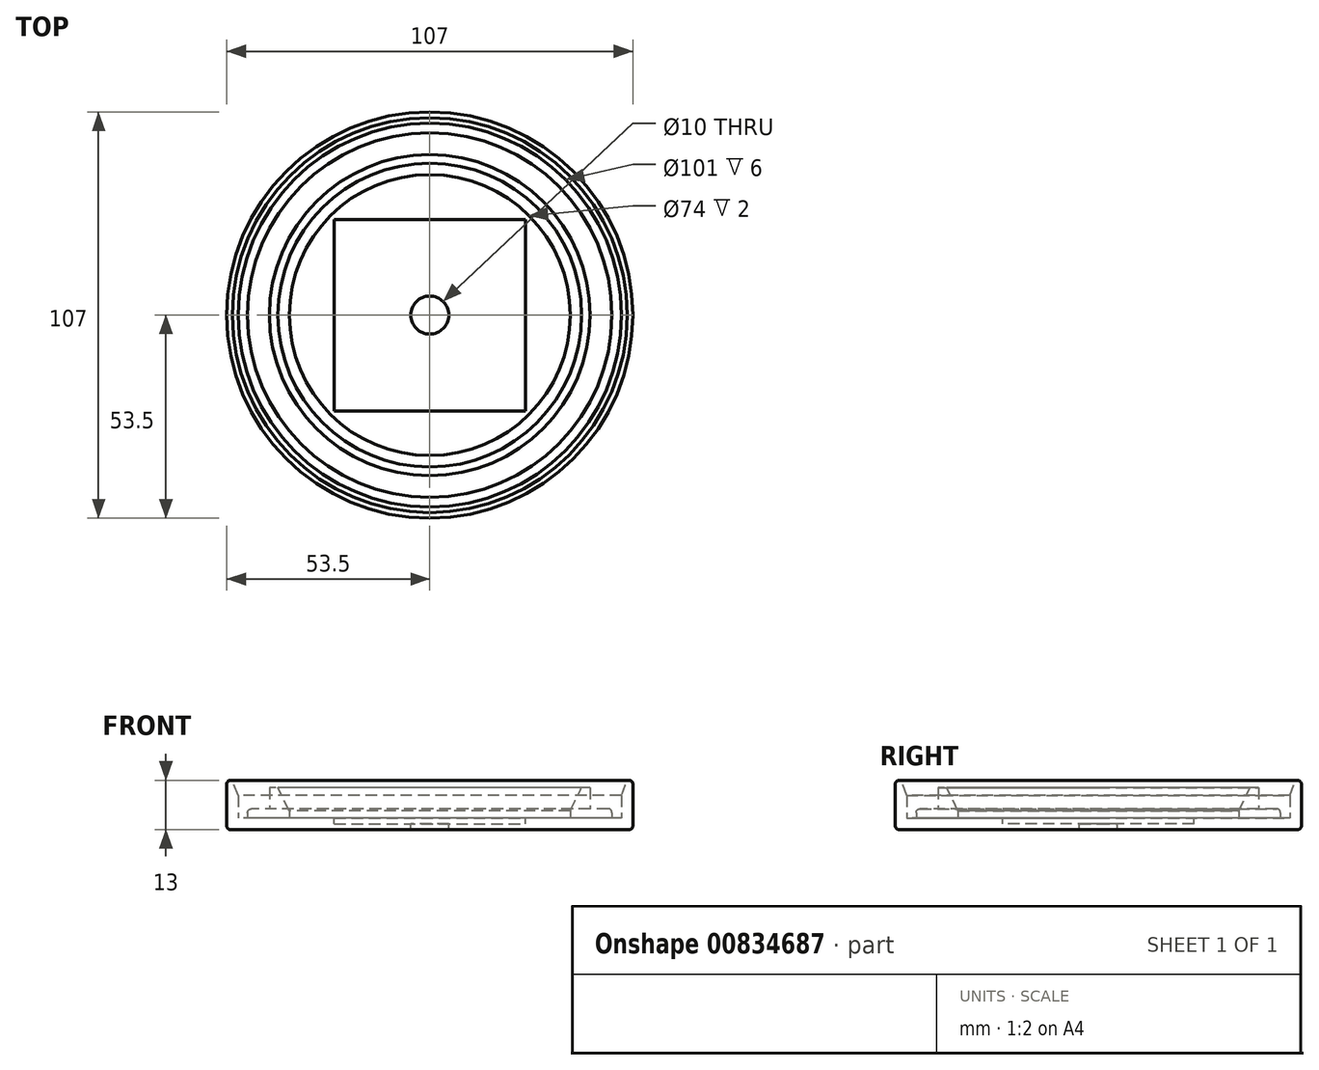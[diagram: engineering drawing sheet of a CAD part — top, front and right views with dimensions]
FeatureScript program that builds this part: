
annotation { "Feature Type Name" : "Feature", "Feature Type Description" : "" }
export const myFeature = defineFeature(function(context is Context, id is Id, definition is map)
    precondition{}
    {
        {
            var Q0;
            Q0=qCreatedBy(makeId("Top.planeOp"),FACE);
            var sketch = newSketch(context, id + "F0", { "sketchPlane" : qUnion([Q0])});
            skCircle(sketch, "E0", {"center": v(0, 0) * mm, "radius": 53.5 * mm});
            skSolve(sketch);
        }
        {
            var Q0;
            Q0=makeQuery(id+"F0.imprint","IMPRINT",FACE,{"disambiguationData":[TD([[makeQuery(id+"F0.imprint","IMPRINT",EDGE,{"derivedFrom":sQuery(id+"F0.wireOp",EDGE,"E0")}),1.0]])]});
            extrude(context, id + "F1", {"entities" : qUnion([Q0]), "depth" : 13 * mm, "offsetDistance" : 25 * mm});
        }
        {
            var Q0;
            Q0=makeQuery(id+"F1.opExtrude","CAP_FACE",FACE,{"disambiguationData":[OSD([sQuery(id+"F0.wireOp",EDGE,"E0")])],"isStart":false});
            shell(context, id + "F2", {"entities" : qUnion([Q0]), "thickness" : 3 * mm});
        }
        {
            var Q0;
            {var subQ0=sQuery(id+"F0.wireOp",EDGE,"E0");Q0=makeQuery(id+"F2.opShell","OFFSET_FACE",FACE,{"disambiguationData":[OSD([subQ0]),TDD([makeQuery(id+"F1.opExtrude","CAP_FACE",FACE,{"disambiguationData":[OSD([subQ0])],"isStart":true})])]});}
            var sketch = newSketch(context, id + "F3", { "sketchPlane" : qUnion([Q0])});
            skCircle(sketch, "E1", {"center": v(0, 0) * mm, "radius": 48 * mm});
            skCircle(sketch, "E2", {"center": v(0, 0) * mm, "radius": 42.25 * mm});
            skCircle(sketch, "E3", {"center": v(0, 0) * mm, "radius": 37 * mm});
            skSolve(sketch);
        }
        {
            var Q0;
            Q0=makeQuery(id+"F3.imprint","IMPRINT",FACE,{"disambiguationData":[TD([[makeQuery(id+"F3.imprint","IMPRINT",EDGE,{"derivedFrom":sQuery(id+"F3.wireOp",EDGE,"E1")}),1.0]])]});
            var Q1;
            Q1=makeQuery(id+"F3.imprint","IMPRINT",FACE,{"disambiguationData":[TD([[makeQuery(id+"F3.imprint","IMPRINT",EDGE,{"derivedFrom":sQuery(id+"F3.wireOp",EDGE,"E2")}),1.0]])]});
            extrude(context, id + "F4", {"entities" : qUnion([Q0, Q1]), "operationType" : NewBodyOperationType.ADD, "depth" : 2.5 * mm, "offsetDistance" : 25 * mm});
        }
        {
            var Q0;
            Q0=makeQuery(id+"F3.imprint","IMPRINT",FACE,{"disambiguationData":[TD([[makeQuery(id+"F3.imprint","IMPRINT",EDGE,{"derivedFrom":sQuery(id+"F3.wireOp",EDGE,"E2")}),1.0]])]});
            extrude(context, id + "F5", {"entities" : qUnion([Q0]), "operationType" : NewBodyOperationType.ADD, "depth" : 8 * mm, "offsetDistance" : 25 * mm});
        }
        {
            var Q0;
            Q0=makeQuery(id+"F5.opExtrude","CAP_EDGE",EDGE,{"disambiguationData":[OSD([sQuery(id+"F3.wireOp",EDGE,"E3")])],"isStart":false});
            chamfer(context, id + "F6", {"entities" : qUnion([Q0]), "chamferType" : ChamferType.TWO_OFFSETS, "width1" : 3 * mm, "oppositeDirection" : true, "width2" : 6 * mm, "tangentPropagation" : true});
        }
        {
            var Q0;
            {var subQ0=sQuery(id+"F0.wireOp",EDGE,"E0");Q0=makeQuery(id+"F2.opShell","OFFSET_EDGE",EDGE,{"disambiguationData":[OSD([subQ0]),TDD([makeQuery(id+"F1.opExtrude","CAP_EDGE",EDGE,{"disambiguationData":[OSD([subQ0])],"isStart":false})])]});}
            chamfer(context, id + "F7", {"entities" : qUnion([Q0]), "chamferType" : ChamferType.TWO_OFFSETS, "width1" : 4 * mm, "oppositeDirection" : false, "width2" : 1.5 * mm, "tangentPropagation" : true});
        }
        {
            var Q0;
            Q0=makeQuery(id+"F4.opExtrude","CAP_EDGE",EDGE,{"disambiguationData":[OSD([sQuery(id+"F3.wireOp",EDGE,"E1")])],"isStart":false});
            var Q1;
            Q1=makeQuery(id+"F1.opExtrude","CAP_EDGE",EDGE,{"disambiguationData":[OSD([sQuery(id+"F0.wireOp",EDGE,"E0")])],"isStart":true});
            var Q2;
            Q2=makeQuery(id+"F1.opExtrude","CAP_EDGE",EDGE,{"disambiguationData":[OSD([sQuery(id+"F0.wireOp",EDGE,"E0")])],"isStart":false});
            fillet(context, id + "F8", {"entities" : qUnion([Q0, Q1, Q2]), "radius" : 1 * mm, "tangentPropagation" : true, "allowEdgeOverflow" : false});
        }
        {
            var Q0;
            Q0=makeQuery(id+"F4.opExtrude","CAP_FACE",FACE,{"disambiguationData":[OSD([sQuery(id+"F3.wireOp",EDGE,"E1")])],"isStart":false});
            var sketch = newSketch(context, id + "F9", { "sketchPlane" : qUnion([Q0])});
            skCircle(sketch, "E4", {"center": v(0, 0) * mm, "radius": 5 * mm});
            skSolve(sketch);
        }
        {
            var Q0;
            Q0=qSketchRegion(id+"F9",true);
            extrude(context, id + "F10", {"entities" : qUnion([Q0]), "operationType" : NewBodyOperationType.REMOVE, "endBound" : BoundingType.SYMMETRIC, "oppositeDirection" : true, "depth" : 91.4 * mm, "offsetDistance" : 25 * mm});
        }
        {
            var Q0;
            Q0=makeQuery(id+"F3.imprint","IMPRINT",FACE,{"disambiguationData":[TD([[makeQuery(id+"F3.imprint","IMPRINT",EDGE,{"derivedFrom":sQuery(id+"F3.wireOp",EDGE,"E3")}),1.0]])]});
            var sketch = newSketch(context, id + "F11", { "sketchPlane" : qUnion([Q0])});
            skLineSegment(sketch, "E5.bottom", {"start": v(-25.2, 25.2) * mm, "end": v(25.2, 25.2) * mm});
            skLineSegment(sketch, "E5.top", {"start": v(-25.2, -25.2) * mm, "end": v(25.2, -25.2) * mm});
            skLineSegment(sketch, "E5.left", {"start": v(-25.2, 25.2) * mm, "end": v(-25.2, -25.2) * mm});
            skLineSegment(sketch, "E5.right", {"start": v(25.2, 25.2) * mm, "end": v(25.2, -25.2) * mm});
            skPoint(sketch, "E5.middle", {"position": v(0, 0) * mm});
            skSolve(sketch);
        }
        {
            var Q0;
            {var subQ1=makeQuery(id+"F3.imprint","IMPRINT",EDGE,{"derivedFrom":sQuery(id+"F3.wireOp",EDGE,"E3")});var subQ10=sQuery(id+"F11.wireOp",EDGE,"E5.bottom");var subQ11=makeQuery(id+"F11.imprint","INTERSECT",VERTEX,{"disambiguationData":[OD(0.0)],"derivedFrom":[subQ1,subQ10]});Q0=makeQuery(id+"F11.imprint","IMPRINT",FACE,{"disambiguationData":[TD([[makeQuery(id+"F11.imprint","IMPRINT",EDGE,{"disambiguationData":[TD([[subQ11,-1.0]])],"derivedFrom":subQ10}),-1.0]])]});}
            extrude(context, id + "F12", {"entities" : qUnion([Q0]), "operationType" : NewBodyOperationType.REMOVE, "oppositeDirection" : true, "depth" : 1.5 * mm, "offsetDistance" : 25 * mm});
        }
    });
